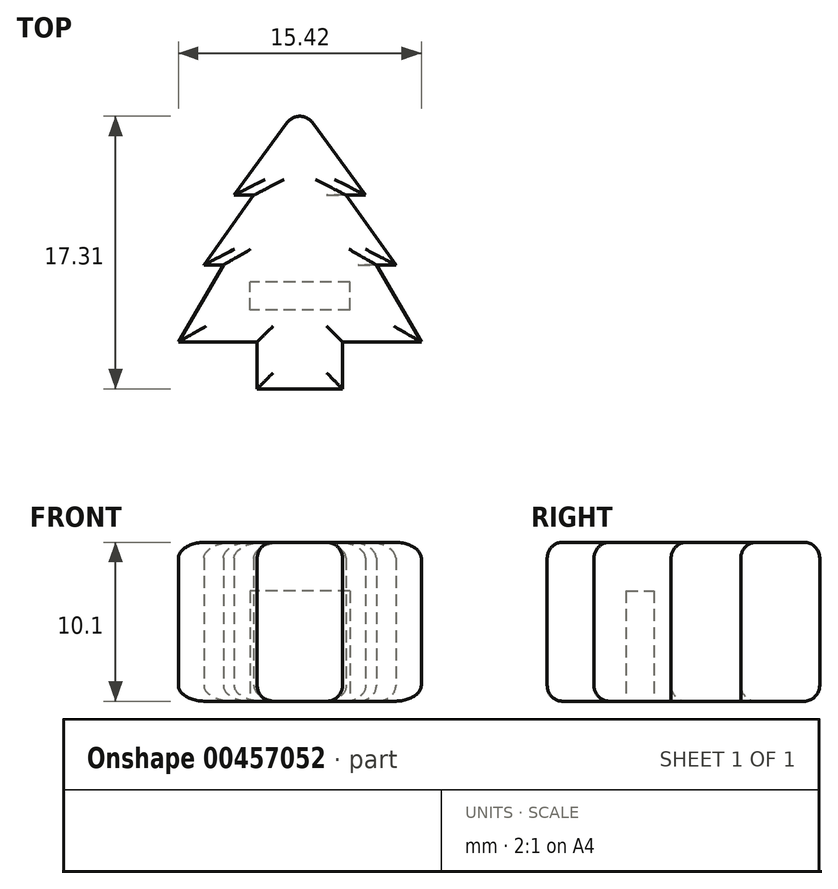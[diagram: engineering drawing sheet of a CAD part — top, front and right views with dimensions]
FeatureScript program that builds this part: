
annotation { "Feature Type Name" : "Feature", "Feature Type Description" : "" }
export const myFeature = defineFeature(function(context is Context, id is Id, definition is map)
    precondition{}
    {
        {
            var Q0;
            Q0=qCreatedBy(makeId("Top.planeOp"),FACE);
            var sketch = newSketch(context, id + "F0", { "sketchPlane" : qUnion([Q0])});
            skLineSegment(sketch, "E0", {"start": v(0, 0) * mm, "end": v(-2.7, 0) * mm});
            skLineSegment(sketch, "E1", {"start": v(-2.7, 0) * mm, "end": v(-2.7, 2.97) * mm});
            skLineSegment(sketch, "E2", {"start": v(-6.1, 7.87) * mm, "end": v(-2.93, 12.3) * mm});
            skLineSegment(sketch, "E3", {"start": v(-2.93, 12.3) * mm, "end": v(-4.17, 12.3) * mm});
            skLineSegment(sketch, "E4", {"start": v(-4.17, 12.3) * mm, "end": v(0, 18) * mm});
            skLineSegment(sketch, "E5", {"start": v(-7.71, 2.97) * mm, "end": v(-2.7, 2.97) * mm});
            skLineSegment(sketch, "E6", {"start": v(0, 18) * mm, "end": v(0, 0) * mm, "construction": true});
            skLineSegment(sketch, "E7.MirrorCS", {"start": v(2.7, 0) * mm, "end": v(2.7, 2.97) * mm});
            skLineSegment(sketch, "E8.MirrorCS", {"start": v(7.71, 2.97) * mm, "end": v(2.7, 2.97) * mm});
            skLineSegment(sketch, "E9.MirrorCS", {"start": v(2.93, 12.3) * mm, "end": v(4.17, 12.3) * mm});
            skLineSegment(sketch, "E10.MirrorCS", {"start": v(6.1, 7.87) * mm, "end": v(2.93, 12.3) * mm});
            skLineSegment(sketch, "E11.MirrorCS", {"start": v(4.17, 12.3) * mm, "end": v(0, 18) * mm});
            skLineSegment(sketch, "E12", {"start": v(0, 0) * mm, "end": v(2.7, 0) * mm});
            skLineSegment(sketch, "E13", {"start": v(6.1, 7.87) * mm, "end": v(4.86, 7.87) * mm});
            skLineSegment(sketch, "E14", {"start": v(4.86, 7.87) * mm, "end": v(7.71, 2.97) * mm});
            skLineSegment(sketch, "E15", {"start": v(-6.1, 7.87) * mm, "end": v(-4.86, 7.87) * mm});
            skLineSegment(sketch, "E16", {"start": v(-4.86, 7.87) * mm, "end": v(-7.71, 2.97) * mm});
            skSolve(sketch);
        }
        {
            var Q0;
            Q0 = qSketchRegion(id + "F0", true);
            extrude(context, id + "F1", {"entities" : qUnion([Q0]), "depth" : 10.1 * mm});
        }
        {
            var Q0;
            Q0=makeQuery(id+"F1.opExtrude","CAP_FACE",FACE,{"disambiguationData":[OSD([sQuery(id+"F0.wireOp",EDGE,"E0"),sQuery(id+"F0.wireOp",EDGE,"E1"),sQuery(id+"F0.wireOp",EDGE,"PuAWzdY3-p6pt-pAHf-Xw98-QD3yTg90dZiT"),sQuery(id+"F0.wireOp",EDGE,"YihKcMxM-6skp-ZjBG-0D1H-7UrPPhsxYa85"),sQuery(id+"F0.wireOp",EDGE,"E2"),sQuery(id+"F0.wireOp",EDGE,"E3"),sQuery(id+"F0.wireOp",EDGE,"E4"),sQuery(id+"F0.wireOp",EDGE,"E5"),sQuery(id+"F0.wireOp",EDGE,"E7.MirrorCS"),sQuery(id+"F0.wireOp",EDGE,"8ccf6dab-e246-473f-9861-874d1259ede91.MirrorCS"),sQuery(id+"F0.wireOp",EDGE,"E8.MirrorCS"),sQuery(id+"F0.wireOp",EDGE,"E9.MirrorCS"),sQuery(id+"F0.wireOp",EDGE,"8ccf6dab-e246-473f-9861-874d1259ede94.MirrorCS"),sQuery(id+"F0.wireOp",EDGE,"E10.MirrorCS"),sQuery(id+"F0.wireOp",EDGE,"E11.MirrorCS"),sQuery(id+"F0.wireOp",EDGE,"E12")])],"isStart":true});
            var sketch = newSketch(context, id + "F2", { "sketchPlane" : qUnion([Q0])});
            skLineSegment(sketch, "E17.bottom", {"start": v(3.18, -5) * mm, "end": v(-3.18, -5) * mm});
            skLineSegment(sketch, "E17.top", {"start": v(3.17, -6.78) * mm, "end": v(-3.17, -6.78) * mm});
            skLineSegment(sketch, "E17.left", {"start": v(3.18, -5) * mm, "end": v(3.18, -6.78) * mm});
            skLineSegment(sketch, "E17.right", {"start": v(-3.18, -5) * mm, "end": v(-3.17, -6.78) * mm});
            skPoint(sketch, "E18", {"position": v(0, -6.78) * mm});
            skSolve(sketch);
        }
        {
            var Q0;
            Q0 = qSketchRegion(id + "F2", true);
            extrude(context, id + "F3", {"entities" : qUnion([Q0]), "operationType" : NewBodyOperationType.REMOVE, "oppositeDirection" : true, "depth" : 4.32 * mm});
        }
        {
            var Q0;
            Q0 = qSketchRegion(id + "F2", true);
            extrude(context, id + "F4", {"entities" : qUnion([Q0]), "operationType" : NewBodyOperationType.REMOVE, "oppositeDirection" : true, "depth" : 7 * mm});
        }
        {
            var Q0;
            Q0=makeQuery(id+"F1.opExtrude","SWEPT_FACE",FACE,{"disambiguationData":[OSD([sQuery(id+"F0.wireOp",EDGE,"E0"),sQuery(id+"F0.wireOp",EDGE,"E12")])]});
            var sketch = newSketch(context, id + "F5", { "sketchPlane" : qUnion([Q0])});
            skLineSegment(sketch, "E19.bottom", {"start": v(-3.17, 4.16) * mm, "end": v(3.18, 4.16) * mm});
            skLineSegment(sketch, "E19.top", {"start": v(-3.18, 5.94) * mm, "end": v(3.17, 5.94) * mm});
            skLineSegment(sketch, "E19.left", {"start": v(-3.17, 4.16) * mm, "end": v(-3.18, 5.94) * mm});
            skLineSegment(sketch, "E19.right", {"start": v(3.18, 4.16) * mm, "end": v(3.17, 5.94) * mm});
            skPoint(sketch, "E19.middle", {"position": v(0, 5.05) * mm});
            skLineSegment(sketch, "E20", {"start": v(0, 0) * mm, "end": v(0, 10.1) * mm});
            skSolve(sketch);
        }
        {
            var Q0;
            Q0=makeQuery(id+"F1.opExtrude","SWEPT_EDGE",EDGE,{"disambiguationData":[OSD([sQuery(id+"F0.wireOp",EDGE,"E4"),sQuery(id+"F0.wireOp",EDGE,"E11.MirrorCS")])]});
            var Q1;
            Q1=makeQuery(id+"F1.opExtrude","CAP_FACE",FACE,{"disambiguationData":[OSD([sQuery(id+"F0.wireOp",EDGE,"E0"),sQuery(id+"F0.wireOp",EDGE,"E1"),sQuery(id+"F0.wireOp",EDGE,"E2"),sQuery(id+"F0.wireOp",EDGE,"E3"),sQuery(id+"F0.wireOp",EDGE,"E4"),sQuery(id+"F0.wireOp",EDGE,"E5"),sQuery(id+"F0.wireOp",EDGE,"E7.MirrorCS"),sQuery(id+"F0.wireOp",EDGE,"E8.MirrorCS"),sQuery(id+"F0.wireOp",EDGE,"E9.MirrorCS"),sQuery(id+"F0.wireOp",EDGE,"E10.MirrorCS"),sQuery(id+"F0.wireOp",EDGE,"E11.MirrorCS"),sQuery(id+"F0.wireOp",EDGE,"E12"),sQuery(id+"F0.wireOp",EDGE,"E13"),sQuery(id+"F0.wireOp",EDGE,"E14"),sQuery(id+"F0.wireOp",EDGE,"E15"),sQuery(id+"F0.wireOp",EDGE,"E16")])],"isStart":false});
            var Q2;
            Q2=makeQuery(id+"F1.opExtrude","CAP_EDGE",EDGE,{"disambiguationData":[OSD([sQuery(id+"F0.wireOp",EDGE,"E10.MirrorCS")])],"isStart":true});
            var Q3;
            Q3=makeQuery(id+"F1.opExtrude","CAP_EDGE",EDGE,{"disambiguationData":[OSD([sQuery(id+"F0.wireOp",EDGE,"E11.MirrorCS")])],"isStart":true});
            var Q4;
            Q4=makeQuery(id+"F1.opExtrude","CAP_EDGE",EDGE,{"disambiguationData":[OSD([sQuery(id+"F0.wireOp",EDGE,"E4")])],"isStart":true});
            var Q5;
            Q5=makeQuery(id+"F1.opExtrude","CAP_EDGE",EDGE,{"disambiguationData":[OSD([sQuery(id+"F0.wireOp",EDGE,"E2")])],"isStart":true});
            var Q6;
            Q6=makeQuery(id+"F1.opExtrude","CAP_EDGE",EDGE,{"disambiguationData":[OSD([sQuery(id+"F0.wireOp",EDGE,"E3")])],"isStart":true});
            var Q7;
            Q7=makeQuery(id+"F1.opExtrude","CAP_EDGE",EDGE,{"disambiguationData":[OSD([sQuery(id+"F0.wireOp",EDGE,"E16")])],"isStart":true});
            var Q8;
            Q8=makeQuery(id+"F1.opExtrude","CAP_EDGE",EDGE,{"disambiguationData":[OSD([sQuery(id+"F0.wireOp",EDGE,"E15")])],"isStart":true});
            var Q9;
            Q9=makeQuery(id+"F1.opExtrude","CAP_EDGE",EDGE,{"disambiguationData":[OSD([sQuery(id+"F0.wireOp",EDGE,"E5")])],"isStart":true});
            var Q10;
            Q10=makeQuery(id+"F1.opExtrude","CAP_EDGE",EDGE,{"disambiguationData":[OSD([sQuery(id+"F0.wireOp",EDGE,"E1")])],"isStart":true});
            var Q11;
            Q11=makeQuery(id+"F1.opExtrude","CAP_EDGE",EDGE,{"disambiguationData":[OSD([sQuery(id+"F0.wireOp",EDGE,"E0"),sQuery(id+"F0.wireOp",EDGE,"E12")])],"isStart":true});
            var Q12;
            Q12=makeQuery(id+"F1.opExtrude","CAP_EDGE",EDGE,{"disambiguationData":[OSD([sQuery(id+"F0.wireOp",EDGE,"E7.MirrorCS")])],"isStart":true});
            var Q13;
            Q13=makeQuery(id+"F1.opExtrude","CAP_EDGE",EDGE,{"disambiguationData":[OSD([sQuery(id+"F0.wireOp",EDGE,"E8.MirrorCS")])],"isStart":true});
            var Q14;
            Q14=makeQuery(id+"F1.opExtrude","CAP_EDGE",EDGE,{"disambiguationData":[OSD([sQuery(id+"F0.wireOp",EDGE,"E14")])],"isStart":true});
            fillet(context, id + "F6", {"entities" : qUnion([Q0, Q1, Q2, Q3, Q4, Q5, Q6, Q7, Q8, Q9, Q10, Q11, Q12, Q13, Q14]), "radius" : 1 * mm, "tangentPropagation" : true, "allowEdgeOverflow" : false});
        }
    });
